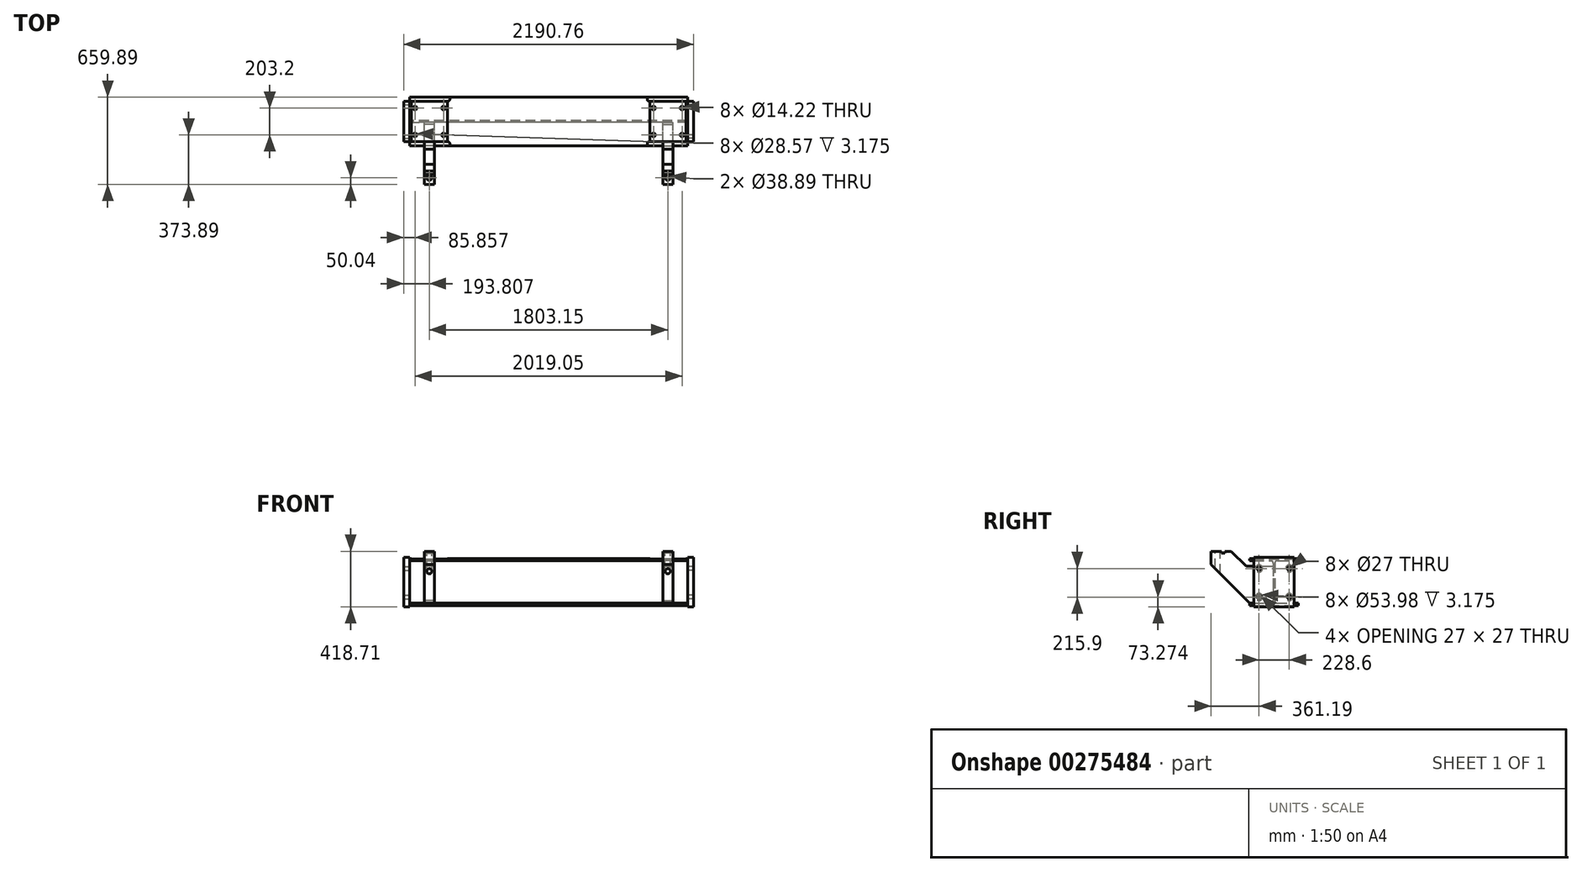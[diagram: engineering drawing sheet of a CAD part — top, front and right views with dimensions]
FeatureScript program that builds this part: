
annotation { "Feature Type Name" : "Feature", "Feature Type Description" : "" }
export const myFeature = defineFeature(function(context is Context, id is Id, definition is map)
    precondition{}
    {
        {
            var Q0;
            Q0=qCreatedBy(makeId("Right.planeOp"),FACE);
            var sketch = newSketch(context, id + "F0", { "sketchPlane" : qUnion([Q0])});
            skLineSegment(sketch, "E0.bottom", {"start": v(-184.4, 178.05) * mm, "end": v(184.4, 178.05) * mm});
            skLineSegment(sketch, "E0.top", {"start": v(-184.4, -178.05) * mm, "end": v(184.4, -178.05) * mm});
            skLineSegment(sketch, "E0.left", {"start": v(-184.4, 178.05) * mm, "end": v(-184.4, 160.02) * mm});
            skLineSegment(sketch, "E0.right", {"start": v(184.4, 178.05) * mm, "end": v(184.4, 160.02) * mm});
            skPoint(sketch, "E0.middle", {"position": v(0, 0) * mm});
            skLineSegment(sketch, "E1", {"start": v(0, 188.74) * mm, "end": v(0, -185.55) * mm, "construction": true});
            skPoint(sketch, "E1.startSnap0", {"position": v(0, 178.05) * mm});
            skLineSegment(sketch, "E2", {"start": v(-233.18, 0) * mm, "end": v(213.64, 0) * mm, "construction": true});
            skLineSegment(sketch, "E3.0", {"start": v(-184.4, 160.02) * mm, "end": v(-23.37, 160.02) * mm});
            skLineSegment(sketch, "E4.MirrorCS", {"start": v(-184.4, -160.02) * mm, "end": v(-23.37, -160.02) * mm});
            skLineSegment(sketch, "E5.0", {"start": v(-5.59, 142.24) * mm, "end": v(-5.59, -142.24) * mm});
            skLineSegment(sketch, "E6.MirrorCS", {"start": v(5.59, 142.24) * mm, "end": v(5.59, -142.24) * mm});
            skPoint(sketch, "E7.orphan", {"position": v(5.59, 188.74) * mm});
            skPoint(sketch, "E8.orphan", {"position": v(-5.59, 188.74) * mm});
            skLineSegment(sketch, "E9.trimOffspring", {"start": v(23.37, 160.02) * mm, "end": v(184.4, 160.02) * mm});
            skLineSegment(sketch, "E10.trimOffspring", {"start": v(-184.4, -160.02) * mm, "end": v(-184.4, -178.05) * mm});
            skLineSegment(sketch, "E11.trimOffspring", {"start": v(184.4, -160.02) * mm, "end": v(184.4, -178.05) * mm});
            skPoint(sketch, "E12.orphan", {"position": v(-5.59, -185.55) * mm});
            skPoint(sketch, "E13.orphan", {"position": v(5.59, -185.55) * mm});
            skLineSegment(sketch, "E14.trimOffspring", {"start": v(23.37, -160.02) * mm, "end": v(184.4, -160.02) * mm});
            skPoint(sketch, "E15.visualSharp", {"position": v(-5.59, -160.02) * mm});
            skArc(sketch, "E15.filletArc", {"start": v(-23.37, -160.02) * mm, "mid": v(-10.8, -154.81) * mm, "end": v(-5.59, -142.24) * mm});
            skPoint(sketch, "E16.visualSharp", {"position": v(5.59, -160.02) * mm});
            skArc(sketch, "E16.filletArc", {"start": v(5.59, -142.24) * mm, "mid": v(10.8, -154.81) * mm, "end": v(23.37, -160.02) * mm});
            skPoint(sketch, "E17.visualSharp", {"position": v(-5.59, 160.02) * mm});
            skArc(sketch, "E17.filletArc", {"start": v(-5.59, 142.24) * mm, "mid": v(-10.8, 154.81) * mm, "end": v(-23.37, 160.02) * mm});
            skPoint(sketch, "E18.visualSharp", {"position": v(5.59, 160.02) * mm});
            skArc(sketch, "E18.filletArc", {"start": v(23.37, 160.02) * mm, "mid": v(10.8, 154.81) * mm, "end": v(5.59, 142.24) * mm});
            skSolve(sketch);
        }
        {
            var Q0;
            Q0 = qSketchRegion(id + "F0", true);
            extrude(context, id + "F1", {"entities" : qUnion([Q0]), "depth" : 1050.92 * mm});
        }
        {
            var Q0;
            Q0=makeQuery(id+"F1.opExtrude","SWEPT_FACE",FACE,{"disambiguationData":[OSD([sQuery(id+"F0.wireOp",EDGE,"E0.bottom")])]});
            var sketch = newSketch(context, id + "F2", { "sketchPlane" : qUnion([Q0])});
            skLineSegment(sketch, "E19.0", {"start": v(1050.93, -184.4) * mm, "end": v(1050.93, 184.4) * mm, "construction": true});
            skLineSegment(sketch, "E20.0", {"start": v(1038.23, -184.4) * mm, "end": v(1038.23, 184.4) * mm});
            skLineSegment(sketch, "E21.0", {"start": v(765.18, -184.4) * mm, "end": v(765.18, 184.4) * mm});
            skSolve(sketch);
        }
        {
            var Q0;
            Q0 = qSketchRegion(id + "F2", true);
            var Q1;
            {var subQ0=sQuery(id+"F2.wireOp",EDGE,"E20.0");Q1=makeQuery(id+"F2.imprint","IMPRINT",FACE,{"disambiguationData":[TD([[makeQuery(id+"F2.imprint","IMPRINT",EDGE,{"derivedFrom":subQ0}),1.0]])]});}
            extrude(context, id + "F3", {"entities" : qUnion([Q0, Q1]), "operationType" : NewBodyOperationType.REMOVE, "oppositeDirection" : true, "depth" : 3.17 * mm});
        }
        {
            var Q0;
            Q0=makeQuery(id+"F3.boolean.opBoolean","COPY",FACE,{"derivedFrom":makeQuery(id+"F3.opExtrude","CAP_FACE",FACE,{"disambiguationData":[OSD([sQuery(id+"F0.wireOp",EDGE,"E0.bottom"),sQuery(id+"F0.wireOp",EDGE,"E0.left"),sQuery(id+"F0.wireOp",EDGE,"E0.right"),sQuery(id+"F2.wireOp",EDGE,"E20.0"),sQuery(id+"F2.wireOp",EDGE,"E21.0")])],"isStart":false})});
            var sketch = newSketch(context, id + "F4", { "sketchPlane" : qUnion([Q0])});
            skLineSegment(sketch, "E22.0", {"start": v(1038.23, -184.4) * mm, "end": v(1038.23, 184.4) * mm, "construction": true});
            skLineSegment(sketch, "E23.0", {"start": v(765.18, -184.4) * mm, "end": v(765.18, 184.4) * mm, "construction": true});
            skLineSegment(sketch, "E24.0", {"start": v(1038.23, 184.4) * mm, "end": v(765.18, 184.4) * mm, "construction": true});
            skLineSegment(sketch, "E25.0", {"start": v(1038.23, -184.4) * mm, "end": v(765.18, -184.4) * mm, "construction": true});
            skLineSegment(sketch, "E26.0", {"start": v(1050.93, -184.4) * mm, "end": v(1050.93, 184.4) * mm, "construction": true});
            skLineSegment(sketch, "E27.0", {"start": v(1009.52, -184.4) * mm, "end": v(1009.52, 184.4) * mm, "construction": true});
            skLineSegment(sketch, "E28.0", {"start": v(793.62, -184.4) * mm, "end": v(793.62, 184.4) * mm, "construction": true});
            skLineSegment(sketch, "E29", {"start": v(793.62, 0) * mm, "end": v(1009.52, 0) * mm, "construction": true});
            skLineSegment(sketch, "E30.0", {"start": v(793.62, -101.6) * mm, "end": v(1009.52, -101.6) * mm, "construction": true});
            skPoint(sketch, "E31", {"position": v(793.62, -101.6) * mm});
            skPoint(sketch, "E32", {"position": v(1009.52, -101.6) * mm});
            skPoint(sketch, "E33.MirrorP", {"position": v(793.62, 101.6) * mm});
            skPoint(sketch, "E34.MirrorP", {"position": v(1009.52, 101.6) * mm});
            skSolve(sketch);
        }
        {
            var Q0;
            Q0=sQuery(id+"F4.wireOp",VERTEX,"E33.MirrorP");
            var Q1;
            Q1=sQuery(id+"F4.wireOp",VERTEX,"E34.MirrorP");
            var Q2;
            Q2=sQuery(id+"F4.wireOp",VERTEX,"E31");
            var Q3;
            Q3=sQuery(id+"F4.wireOp",VERTEX,"E32");
            var Q4;
            Q4=makeQuery(id+"F1.opExtrude","SWEPT_BODY",BODY,{"disambiguationData":[OSD([sQuery(id+"F0.wireOp",EDGE,"E0.bottom"),sQuery(id+"F0.wireOp",EDGE,"E0.top"),sQuery(id+"F0.wireOp",EDGE,"E0.left"),sQuery(id+"F0.wireOp",EDGE,"E0.right"),sQuery(id+"F0.wireOp",EDGE,"E3.0"),sQuery(id+"F0.wireOp",EDGE,"E4.MirrorCS"),sQuery(id+"F0.wireOp",EDGE,"E5.0"),sQuery(id+"F0.wireOp",EDGE,"E6.MirrorCS"),sQuery(id+"F0.wireOp",EDGE,"E9.trimOffspring"),sQuery(id+"F0.wireOp",EDGE,"E10.trimOffspring"),sQuery(id+"F0.wireOp",EDGE,"E11.trimOffspring"),sQuery(id+"F0.wireOp",EDGE,"E14.trimOffspring"),sQuery(id+"F0.wireOp",EDGE,"E15.filletArc"),sQuery(id+"F0.wireOp",EDGE,"E16.filletArc"),sQuery(id+"F0.wireOp",EDGE,"E17.filletArc"),sQuery(id+"F0.wireOp",EDGE,"E18.filletArc")])]});
            hole(context, id + "F5", {"style" : HoleStyle.C_BORE, "endStyle" : HoleEndStyle.BLIND, "holeDiameter" : 14.22 * mm, "cBoreDiameter" : 28.57 * mm, "cBoreDepth" : 3.17 * mm, "holeDepth" : 31.75 * mm, "tappedDepth" : 24.82 * mm, "tapClearance" : 3, "startFromSketch" : true, "locations" : qUnion([Q0, Q1, Q2, Q3]), "scope" : qUnion([Q4])});
        }
        {
            var Q0;
            {var subQ2=sQuery(id+"F0.wireOp",EDGE,"E0.bottom");Q0=makeQuery(id+"F3.boolean.opBoolean","SPLIT",FACE,{"disambiguationData":[TD([makeQuery(id+"F3.opExtrude","SWEPT_FACE",FACE,{"disambiguationData":[OSD([sQuery(id+"F2.wireOp",EDGE,"E21.0")])]})])],"derivedFrom":makeQuery(id+"F1.opExtrude","SWEPT_FACE",FACE,{"disambiguationData":[OSD([subQ2])]})});}
            var sketch = newSketch(context, id + "F6", { "sketchPlane" : qUnion([Q0])});
            skLineSegment(sketch, "E35.0", {"start": v(1050.93, -184.4) * mm, "end": v(1050.93, 184.4) * mm, "construction": true});
            skLineSegment(sketch, "E36.bottom", {"start": v(1050.93, 184.4) * mm, "end": v(746.13, 184.4) * mm});
            skLineSegment(sketch, "E36.top", {"start": v(1050.93, 152.65) * mm, "end": v(746.13, 152.65) * mm});
            skLineSegment(sketch, "E36.left", {"start": v(1050.93, 184.4) * mm, "end": v(1050.93, 152.65) * mm});
            skLineSegment(sketch, "E36.right", {"start": v(746.13, 184.4) * mm, "end": v(746.13, 152.65) * mm});
            skLineSegment(sketch, "E37", {"start": v(1050.93, 0) * mm, "end": v(624.94, 0) * mm, "construction": true});
            skPoint(sketch, "E37.endSnap0", {"position": v(1050.93, 0) * mm});
            skLineSegment(sketch, "E38.MirrorCS", {"start": v(1050.93, -184.4) * mm, "end": v(746.13, -184.4) * mm});
            skLineSegment(sketch, "E39.MirrorCS", {"start": v(1050.93, -152.65) * mm, "end": v(746.13, -152.65) * mm});
            skLineSegment(sketch, "E40.MirrorCS", {"start": v(1050.93, -184.4) * mm, "end": v(1050.93, -152.65) * mm});
            skLineSegment(sketch, "E41.MirrorCS", {"start": v(746.13, -184.4) * mm, "end": v(746.13, -152.65) * mm});
            skSolve(sketch);
        }
        {
            var Q0;
            Q0 = qSketchRegion(id + "F6", true);
            extrude(context, id + "F7", {"entities" : qUnion([Q0]), "operationType" : NewBodyOperationType.REMOVE, "oppositeDirection" : true, "depth" : 25.4 * mm});
        }
        {
            var Q0;
            Q0=makeQuery(id+"F7.boolean.opBoolean","COPY",EDGE,{"derivedFrom":makeQuery(id+"F7.opExtrude","SWEPT_EDGE",EDGE,{"disambiguationData":[OSD([sQuery(id+"F6.wireOp",EDGE,"E39.MirrorCS"),sQuery(id+"F6.wireOp",EDGE,"E41.MirrorCS")])]})});
            var Q1;
            Q1=makeQuery(id+"F7.boolean.opBoolean","COPY",EDGE,{"derivedFrom":makeQuery(id+"F7.opExtrude","SWEPT_EDGE",EDGE,{"disambiguationData":[OSD([sQuery(id+"F6.wireOp",EDGE,"E36.top"),sQuery(id+"F6.wireOp",EDGE,"E36.right")])]})});
            fillet(context, id + "F8", {"entities" : qUnion([Q0, Q1]), "radius" : 15.88 * mm, "tangentPropagation" : true, "allowEdgeOverflow" : false});
        }
        {
            var Q0;
            Q0=makeQuery(id+"F1.opExtrude","CAP_FACE",FACE,{"disambiguationData":[OSD([sQuery(id+"F0.wireOp",EDGE,"E0.bottom"),sQuery(id+"F0.wireOp",EDGE,"E0.top"),sQuery(id+"F0.wireOp",EDGE,"E0.left"),sQuery(id+"F0.wireOp",EDGE,"E0.right"),sQuery(id+"F0.wireOp",EDGE,"E3.0"),sQuery(id+"F0.wireOp",EDGE,"E4.MirrorCS"),sQuery(id+"F0.wireOp",EDGE,"E5.0"),sQuery(id+"F0.wireOp",EDGE,"E6.MirrorCS"),sQuery(id+"F0.wireOp",EDGE,"E9.trimOffspring"),sQuery(id+"F0.wireOp",EDGE,"E10.trimOffspring"),sQuery(id+"F0.wireOp",EDGE,"E11.trimOffspring"),sQuery(id+"F0.wireOp",EDGE,"E14.trimOffspring"),sQuery(id+"F0.wireOp",EDGE,"E15.filletArc"),sQuery(id+"F0.wireOp",EDGE,"E16.filletArc"),sQuery(id+"F0.wireOp",EDGE,"E17.filletArc"),sQuery(id+"F0.wireOp",EDGE,"E18.filletArc")])],"isStart":false});
            var sketch = newSketch(context, id + "F9", { "sketchPlane" : qUnion([Q0])});
            skLineSegment(sketch, "E42.0", {"start": v(-152.65, 178.05) * mm, "end": v(152.65, 178.05) * mm, "construction": true});
            skLineSegment(sketch, "E43.0", {"start": v(-184.4, -178.05) * mm, "end": v(184.4, -178.05) * mm, "construction": true});
            skLineSegment(sketch, "E44", {"start": v(0, 178.05) * mm, "end": v(0, -178.05) * mm, "construction": true});
            skLineSegment(sketch, "E45.bottom", {"start": v(152.4, 187.33) * mm, "end": v(-152.4, 187.33) * mm});
            skLineSegment(sketch, "E45.top", {"start": v(152.4, -187.32) * mm, "end": v(-152.4, -187.32) * mm});
            skLineSegment(sketch, "E45.left", {"start": v(152.4, 187.33) * mm, "end": v(152.4, -187.32) * mm});
            skLineSegment(sketch, "E45.right", {"start": v(-152.4, 187.33) * mm, "end": v(-152.4, -187.32) * mm});
            skPoint(sketch, "E45.middle", {"position": v(0, 0) * mm});
            skSolve(sketch);
        }
        {
            var Q0;
            Q0 = qSketchRegion(id + "F9", true);
            extrude(context, id + "F10", {"entities" : qUnion([Q0]), "depth" : 44.45 * mm});
        }
        {
            var Q0;
            Q0=makeQuery(id+"F10.opExtrude","CAP_FACE",FACE,{"disambiguationData":[OSD([sQuery(id+"F9.wireOp",EDGE,"E45.bottom"),sQuery(id+"F9.wireOp",EDGE,"E45.top"),sQuery(id+"F9.wireOp",EDGE,"E45.left"),sQuery(id+"F9.wireOp",EDGE,"E45.right")])],"isStart":true});
            var sketch = newSketch(context, id + "F11", { "sketchPlane" : qUnion([Q0])});
            skLineSegment(sketch, "E46", {"start": v(0, 231.94) * mm, "end": v(0, -223.02) * mm, "construction": true});
            skLineSegment(sketch, "E47", {"start": v(-209.64, 0) * mm, "end": v(204.44, 0) * mm, "construction": true});
            skLineSegment(sketch, "E48.0", {"start": v(184.4, 178.05) * mm, "end": v(-184.4, 178.05) * mm, "construction": true});
            skLineSegment(sketch, "E49.0", {"start": v(184.4, 101.85) * mm, "end": v(-184.4, 101.85) * mm, "construction": true});
            skLineSegment(sketch, "E50.0", {"start": v(184.4, -114.05) * mm, "end": v(-184.4, -114.05) * mm, "construction": true});
            skLineSegment(sketch, "E51.0", {"start": v(114.3, 231.94) * mm, "end": v(114.3, -223.02) * mm, "construction": true});
            skPoint(sketch, "E52", {"position": v(114.3, 101.85) * mm});
            skPoint(sketch, "E53", {"position": v(114.3, -114.05) * mm});
            skPoint(sketch, "E54.MirrorP", {"position": v(-114.3, 101.85) * mm});
            skPoint(sketch, "E55.MirrorP", {"position": v(-114.3, -114.05) * mm});
            skSolve(sketch);
        }
        {
            var Q0;
            Q0=sQuery(id+"F11.wireOp",VERTEX,"E54.MirrorP");
            var Q1;
            Q1=sQuery(id+"F11.wireOp",VERTEX,"E55.MirrorP");
            var Q2;
            Q2=sQuery(id+"F11.wireOp",VERTEX,"E52");
            var Q3;
            Q3=sQuery(id+"F11.wireOp",VERTEX,"E53");
            var Q4;
            Q4=makeQuery(id+"F10.opExtrude","SWEPT_BODY",BODY,{"disambiguationData":[OSD([sQuery(id+"F9.wireOp",EDGE,"E45.bottom"),sQuery(id+"F9.wireOp",EDGE,"E45.top"),sQuery(id+"F9.wireOp",EDGE,"E45.left"),sQuery(id+"F9.wireOp",EDGE,"E45.right")])]});
            hole(context, id + "F12", {"style" : HoleStyle.C_BORE, "endStyle" : HoleEndStyle.THROUGH, "holeDiameter" : 27 * mm, "cBoreDiameter" : 53.97 * mm, "cBoreDepth" : 3.17 * mm, "tappedDepth" : 24.82 * mm, "tapClearance" : 3, "startFromSketch" : true, "locations" : qUnion([Q0, Q1, Q2, Q3]), "scope" : qUnion([Q4])});
        }
        {
            var Q0;
            Q0=makeQuery(id+"F1.opExtrude","CAP_FACE",FACE,{"disambiguationData":[OSD([sQuery(id+"F0.wireOp",EDGE,"E0.bottom"),sQuery(id+"F0.wireOp",EDGE,"E0.top"),sQuery(id+"F0.wireOp",EDGE,"E0.left"),sQuery(id+"F0.wireOp",EDGE,"E0.right"),sQuery(id+"F0.wireOp",EDGE,"E3.0"),sQuery(id+"F0.wireOp",EDGE,"E4.MirrorCS"),sQuery(id+"F0.wireOp",EDGE,"E5.0"),sQuery(id+"F0.wireOp",EDGE,"E6.MirrorCS"),sQuery(id+"F0.wireOp",EDGE,"E9.trimOffspring"),sQuery(id+"F0.wireOp",EDGE,"E10.trimOffspring"),sQuery(id+"F0.wireOp",EDGE,"E11.trimOffspring"),sQuery(id+"F0.wireOp",EDGE,"E14.trimOffspring"),sQuery(id+"F0.wireOp",EDGE,"E15.filletArc"),sQuery(id+"F0.wireOp",EDGE,"E16.filletArc"),sQuery(id+"F0.wireOp",EDGE,"E17.filletArc"),sQuery(id+"F0.wireOp",EDGE,"E18.filletArc")])],"isStart":false});
            cPlane(context, id + "F13", {"entities" : qUnion([Q0]), "cplaneType" : CPlaneType.OFFSET, "offset" : 111.25 * mm, "oppositeDirection" : true, "width" : 152.4 * mm, "height" : 152.4 * mm});
        }
        {
            var Q0;
            Q0=qCreatedBy(id+"F13.planeOp",FACE);
            var sketch = newSketch(context, id + "F14", { "sketchPlane" : qUnion([Q0])});
            skLineSegment(sketch, "E56.0", {"start": v(-5.59, 119.38) * mm, "end": v(-5.59, -142.24) * mm});
            skLineSegment(sketch, "E57.0", {"start": v(-184.4, -160.02) * mm, "end": v(-23.37, -160.02) * mm});
            skLineSegment(sketch, "E58.0", {"start": v(-475.49, 231.4) * mm, "end": v(-475.49, 131.06) * mm});
            skLineSegment(sketch, "E59.0", {"start": v(-323.09, 231.4) * mm, "end": v(-323.09, -142.24) * mm, "construction": true});
            skLineSegment(sketch, "E60.0", {"start": v(-475.49, 231.4) * mm, "end": v(-323.09, 231.4) * mm});
            skLineSegment(sketch, "E61", {"start": v(-184.4, -160.02) * mm, "end": v(-475.49, 131.06) * mm});
            skLineSegment(sketch, "E62", {"start": v(-323.09, 231.4) * mm, "end": v(-211.07, 119.38) * mm});
            skLineSegment(sketch, "E63.0", {"start": v(-211.07, 119.38) * mm, "end": v(-5.59, 119.38) * mm});
            skLineSegment(sketch, "E64", {"start": v(-23.37, -160.02) * mm, "end": v(-5.59, -142.24) * mm});
            skPoint(sketch, "E65.orphan", {"position": v(-5.59, 142.24) * mm});
            skSolve(sketch);
        }
        {
            var Q0;
            Q0 = qSketchRegion(id + "F14", true);
            extrude(context, id + "F15", {"entities" : qUnion([Q0]), "oppositeDirection" : true, "depth" : 76.2 * mm});
        }
        {
            var Q0;
            Q0=makeQuery(id+"F15.opExtrude","SWEPT_FACE",FACE,{"disambiguationData":[OSD([sQuery(id+"F14.wireOp",EDGE,"E60.0")])]});
            var sketch = newSketch(context, id + "F16", { "sketchPlane" : qUnion([Q0])});
            skCircle(sketch, "E66.0", {"center": v(1009.52, -101.6) * mm, "radius": 14.29 * mm, "construction": true});
            skLineSegment(sketch, "E67", {"start": v(1009.52, -101.6) * mm, "end": v(827.02, -101.6) * mm, "construction": true});
            skLineSegment(sketch, "E68", {"start": v(901.57, -475.49) * mm, "end": v(901.57, -256.44) * mm, "construction": true});
            skLineSegment(sketch, "E69.0", {"start": v(1009.52, -425.45) * mm, "end": v(827.02, -425.45) * mm, "construction": true});
            skPoint(sketch, "E70", {"position": v(901.57, -425.45) * mm});
            skSolve(sketch);
        }
        {
            var Q0;
            Q0=sQuery(id+"F16.wireOp",VERTEX,"E70");
            var Q1;
            Q1=makeQuery(id+"F15.opExtrude","SWEPT_BODY",BODY,{"disambiguationData":[OSD([sQuery(id+"F14.wireOp",EDGE,"E56.0"),sQuery(id+"F14.wireOp",EDGE,"E57.0"),sQuery(id+"F14.wireOp",EDGE,"E58.0"),sQuery(id+"F14.wireOp",EDGE,"E60.0"),sQuery(id+"F14.wireOp",EDGE,"E61"),sQuery(id+"F14.wireOp",EDGE,"E62"),sQuery(id+"F14.wireOp",EDGE,"E63.0"),sQuery(id+"F14.wireOp",EDGE,"E64")])]});
            hole(context, id + "F17", {"style" : HoleStyle.SIMPLE, "endStyle" : HoleEndStyle.THROUGH, "standardTappedOrClearance" : lookupTablePath({ "standard" : "ANSI", "fit" : "Normal (ASME)", "size" : "1 1/2", "type" : "Clearance" }), "standardBlindInLast" : lookupTablePath({ "fit" : "Free", "standard" : "ANSI", "size" : "1 1/2", "type" : "Clearance" }), "holeDiameter" : 38.9 * mm, "tappedDepth" : 24.82 * mm, "tapClearance" : 3, "startFromSketch" : true, "locations" : qUnion([Q0]), "scope" : qUnion([Q1])});
        }
        {
            var Q0;
            Q0=makeQuery(id+"F15.opExtrude","SWEPT_FACE",FACE,{"disambiguationData":[OSD([sQuery(id+"F14.wireOp",EDGE,"E60.0")])]});
            var sketch = newSketch(context, id + "F18", { "sketchPlane" : qUnion([Q0])});
            skCircle(sketch, "E71.0", {"center": v(901.57, -425.45) * mm, "radius": 19.45 * mm, "construction": true});
            skLineSegment(sketch, "E72", {"start": v(901.57, -425.45) * mm, "end": v(993.5, -425.45) * mm, "construction": true});
            skLineSegment(sketch, "E73.0", {"start": v(901.57, -398.48) * mm, "end": v(939.67, -398.48) * mm, "construction": true});
            skLineSegment(sketch, "E74.0", {"start": v(939.67, -475.49) * mm, "end": v(939.67, -323.09) * mm, "construction": true});
            skLineSegment(sketch, "E75.bottom", {"start": v(939.67, -398.48) * mm, "end": v(863.47, -398.48) * mm});
            skLineSegment(sketch, "E75.top", {"start": v(939.67, -373.08) * mm, "end": v(863.47, -373.08) * mm});
            skLineSegment(sketch, "E75.left", {"start": v(939.67, -398.48) * mm, "end": v(939.67, -373.08) * mm});
            skLineSegment(sketch, "E75.right", {"start": v(863.47, -398.48) * mm, "end": v(863.47, -373.08) * mm});
            skSolve(sketch);
        }
        {
            var Q0;
            Q0 = qSketchRegion(id + "F18", true);
            extrude(context, id + "F19", {"entities" : qUnion([Q0]), "operationType" : NewBodyOperationType.REMOVE, "oppositeDirection" : true, "depth" : 12.7 * mm});
        }
        {
            var Q0;
            Q0=makeQuery(id+"F1.opExtrude","SWEPT_BODY",BODY,{"disambiguationData":[OSD([sQuery(id+"F0.wireOp",EDGE,"E0.bottom"),sQuery(id+"F0.wireOp",EDGE,"E0.top"),sQuery(id+"F0.wireOp",EDGE,"E0.left"),sQuery(id+"F0.wireOp",EDGE,"E0.right"),sQuery(id+"F0.wireOp",EDGE,"E3.0"),sQuery(id+"F0.wireOp",EDGE,"E4.MirrorCS"),sQuery(id+"F0.wireOp",EDGE,"E5.0"),sQuery(id+"F0.wireOp",EDGE,"E6.MirrorCS"),sQuery(id+"F0.wireOp",EDGE,"E9.trimOffspring"),sQuery(id+"F0.wireOp",EDGE,"E10.trimOffspring"),sQuery(id+"F0.wireOp",EDGE,"E11.trimOffspring"),sQuery(id+"F0.wireOp",EDGE,"E14.trimOffspring"),sQuery(id+"F0.wireOp",EDGE,"E15.filletArc"),sQuery(id+"F0.wireOp",EDGE,"E16.filletArc"),sQuery(id+"F0.wireOp",EDGE,"E17.filletArc"),sQuery(id+"F0.wireOp",EDGE,"E18.filletArc")])]});
            var Q1;
            Q1=makeQuery(id+"F15.opExtrude","SWEPT_BODY",BODY,{"disambiguationData":[OSD([sQuery(id+"F14.wireOp",EDGE,"E56.0"),sQuery(id+"F14.wireOp",EDGE,"E57.0"),sQuery(id+"F14.wireOp",EDGE,"E58.0"),sQuery(id+"F14.wireOp",EDGE,"E60.0"),sQuery(id+"F14.wireOp",EDGE,"E61"),sQuery(id+"F14.wireOp",EDGE,"E62"),sQuery(id+"F14.wireOp",EDGE,"E63.0"),sQuery(id+"F14.wireOp",EDGE,"E64")])]});
            var Q2;
            Q2=makeQuery(id+"F10.opExtrude","SWEPT_BODY",BODY,{"disambiguationData":[OSD([sQuery(id+"F9.wireOp",EDGE,"E45.bottom"),sQuery(id+"F9.wireOp",EDGE,"E45.top"),sQuery(id+"F9.wireOp",EDGE,"E45.left"),sQuery(id+"F9.wireOp",EDGE,"E45.right")])]});
            var Q3;
            Q3=qCreatedBy(makeId("Right.planeOp"),FACE);
            mirror(context, id + "F20", {"operationType" : NewBodyOperationType.ADD, "entities" : qUnion([Q0, Q1, Q2]), "mirrorPlane" : qUnion([Q3])});
        }
    });
